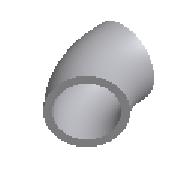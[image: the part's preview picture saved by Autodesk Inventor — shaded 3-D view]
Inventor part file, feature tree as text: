
AUTODESK INVENTOR PART (.ipt)
format: ipt  version: 2024.2 (Build 282272000, 272)  size: 178,688 bytes
history: native  units: mm (DEFAULTED — no unit token found)
features: other x4, sweep x1
ambient origin geometry x8: Origin, YZ Plane, XZ Plane, XY Plane, X Axis, Y Axis, Z Axis, Center Point
bodies: Solid1 (feature_tree)
feature tree (5):
  sweep  "Sweep1"
  other  "Work Point1"
  other  "Work Point2"
  other  "Work Axis1"
  other  "Work Axis2"
